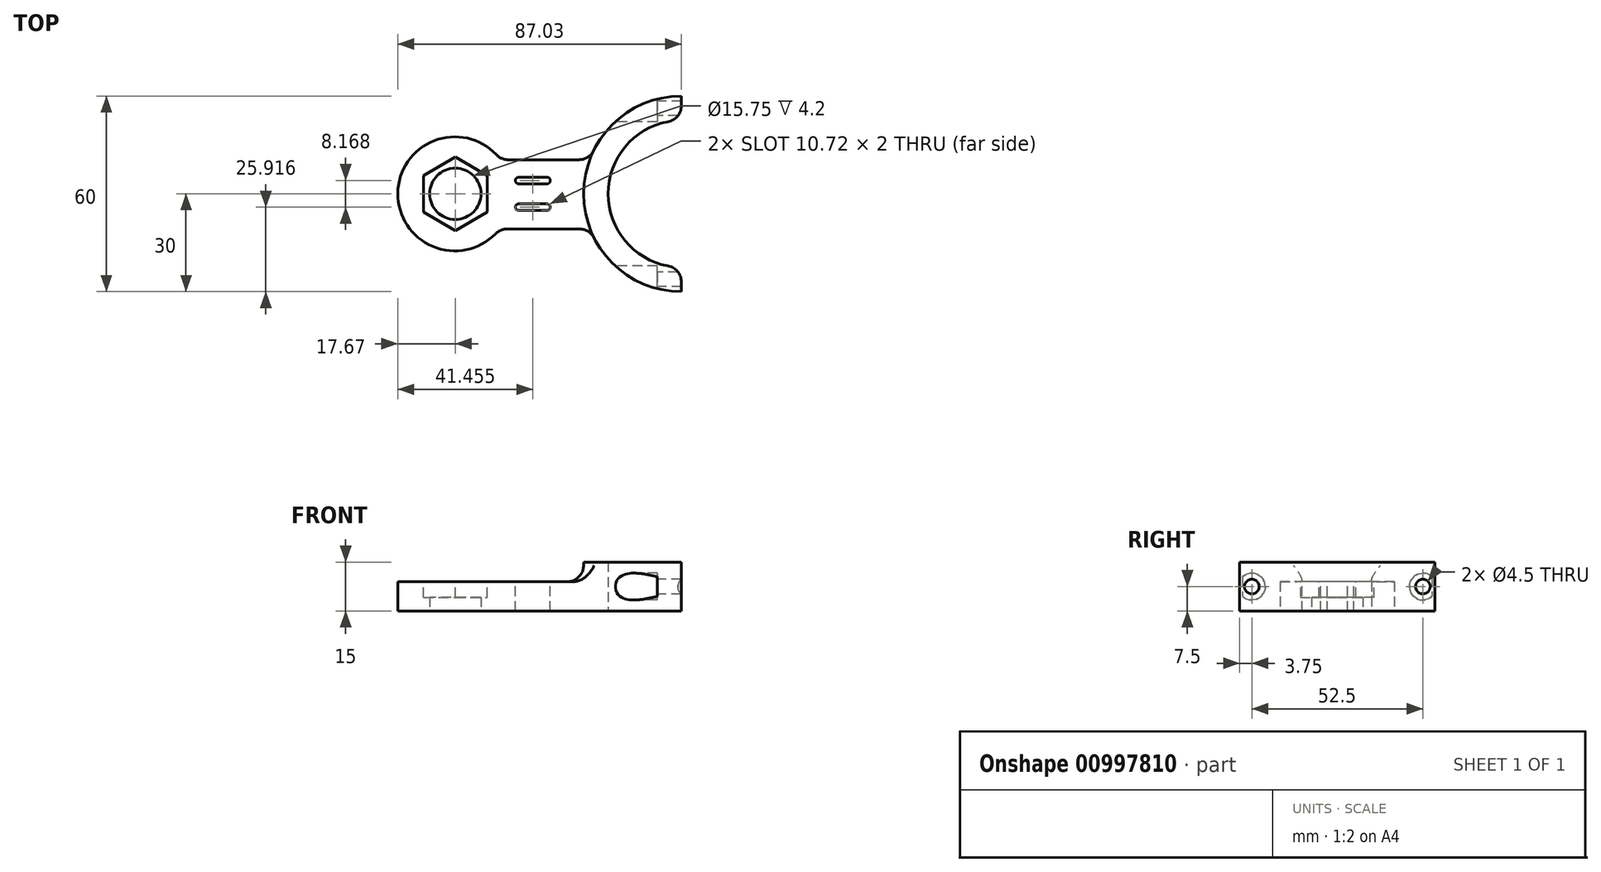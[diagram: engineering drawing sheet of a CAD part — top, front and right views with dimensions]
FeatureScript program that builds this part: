
annotation { "Feature Type Name" : "Feature", "Feature Type Description" : "" }
export const myFeature = defineFeature(function(context is Context, id is Id, definition is map)
    precondition{}
    {
        {
            var Q0;
            Q0=qCreatedBy(makeId("Top.planeOp"),FACE);
            var sketch = newSketch(context, id + "F0", { "sketchPlane" : qUnion([Q0])});
            skCircle(sketch, "E0", {"center": v(0, 0) * mm, "radius": 7.88 * mm});
            skLineSegment(sketch, "E1.top", {"start": v(13.6, -10.8) * mm, "end": v(41.37, -10.8) * mm});
            skArc(sketch, "E2", {"start": v(13.85, 10.47) * mm, "mid": v(-17.67, 0.2) * mm, "end": v(13.6, -10.8) * mm});
            skLineSegment(sketch, "E3", {"start": v(13.85, 10.47) * mm, "end": v(41.25, 10.47) * mm});
            skArc(sketch, "E4", {"start": v(69.36, 22.5) * mm, "mid": v(46.86, 0) * mm, "end": v(69.36, -22.5) * mm});
            skArc(sketch, "E5.0", {"start": v(41.37, -10.8) * mm, "mid": v(52.4, -24.74) * mm, "end": v(69.36, -30) * mm});
            skLineSegment(sketch, "E6", {"start": v(69.36, -22.5) * mm, "end": v(69.36, -30) * mm});
            skLineSegment(sketch, "E7.MirrorCS", {"start": v(69.36, 22.5) * mm, "end": v(69.36, 30) * mm});
            skArc(sketch, "E8.trimOffspring", {"start": v(69.36, 30) * mm, "mid": v(44.63, 16.97) * mm, "end": v(41.37, -10.8) * mm});
            skSolve(sketch);
        }
        {
            var Q0;
            Q0 = qSketchRegion(id + "F0", true);
            extrude(context, id + "F1", {"entities" : qUnion([Q0]), "depth" : 9 * mm, "offsetDistance" : 25 * mm});
        }
        {
            var Q0;
            Q0=makeQuery(id+"F1.opExtrude","CAP_FACE",FACE,{"disambiguationData":[OSD([sQuery(id+"F0.wireOp",EDGE,"E0"),sQuery(id+"F0.wireOp",EDGE,"26NPetrQ-JWbV-A0U1-Rfha-0d6lAM55pXle")])],"isStart":false});
            var sketch = newSketch(context, id + "F2", { "sketchPlane" : qUnion([Q0])});
            skCircle(sketch, "E9.cCircle", {"center": v(0, 0) * mm, "radius": 14.84 * mm, "construction": true});
            skCircle(sketch, "E10.cCircle", {"center": v(0, 0) * mm, "radius": 11.26 * mm, "construction": true});
            skLineSegment(sketch, "E10.0", {"start": v(9.75, 5.63) * mm, "end": v(9.75, -5.63) * mm});
            skLineSegment(sketch, "E10.1", {"start": v(9.75, -5.63) * mm, "end": v(0, -11.26) * mm});
            skLineSegment(sketch, "E10.2", {"start": v(0, -11.26) * mm, "end": v(-9.75, -5.63) * mm});
            skLineSegment(sketch, "E10.3", {"start": v(-9.75, -5.63) * mm, "end": v(-9.75, 5.63) * mm});
            skLineSegment(sketch, "E10.4", {"start": v(-9.75, 5.63) * mm, "end": v(0, 11.26) * mm});
            skLineSegment(sketch, "E10.5", {"start": v(0, 11.26) * mm, "end": v(9.75, 5.63) * mm});
            skSolve(sketch);
        }
        {
            var Q0;
            Q0=makeQuery(id+"F2.imprint","IMPRINT",FACE,{"disambiguationData":[TD([[makeQuery(id+"F2.imprint","IMPRINT",EDGE,{"derivedFrom":sQuery(id+"F2.wireOp",EDGE,"E10.0")}),-1.0]])]});
            extrude(context, id + "F3", {"entities" : qUnion([Q0]), "operationType" : NewBodyOperationType.REMOVE, "oppositeDirection" : true, "depth" : 4.8 * mm, "offsetDistance" : 25 * mm});
        }
        {
            var Q0;
            Q0=makeQuery(id+"F0.imprint","IMPRINT",FACE,{"disambiguationData":[TD([[makeQuery(id+"F0.imprint","IMPRINT",EDGE,{"derivedFrom":sQuery(id+"F0.wireOp",EDGE,"E4")}),-1.0]])]});
            extrude(context, id + "F4", {"entities" : qUnion([Q0]), "operationType" : NewBodyOperationType.ADD, "depth" : 15 * mm, "offsetDistance" : 25 * mm});
        }
        {
            var Q0;
            Q0=makeQuery(id+"F1.opExtrude","SWEPT_EDGE",EDGE,{"disambiguationData":[OSD([sQuery(id+"F0.wireOp",EDGE,"E1.bottom"),sQuery(id+"F0.wireOp",EDGE,"E2")])]});
            var Q1;
            Q1=makeQuery(id+"F1.opExtrude","SWEPT_EDGE",EDGE,{"disambiguationData":[OSD([sQuery(id+"F0.wireOp",EDGE,"E1.top"),sQuery(id+"F0.wireOp",EDGE,"E2")])]});
            var Q2;
            Q2=makeQuery(id+"F1.opExtrude","SWEPT_EDGE",EDGE,{"disambiguationData":[OSD([sQuery(id+"F0.wireOp",EDGE,"E3"),sQuery(id+"F0.wireOp",EDGE,"E8.trimOffspring")])]});
            var Q3;
            Q3=makeQuery(id+"F1.opExtrude","SWEPT_EDGE",EDGE,{"disambiguationData":[OSD([sQuery(id+"F0.wireOp",EDGE,"E1.top"),sQuery(id+"F0.wireOp",EDGE,"E5.0"),sQuery(id+"F0.wireOp",EDGE,"E8.trimOffspring")])]});
            var Q4;
            {var subQ0=sQuery(id+"F0.wireOp",EDGE,"E8.trimOffspring");var subQ1=sQuery(id+"F0.wireOp",EDGE,"E5.0");Q4=makeQuery(id+"F4.boolean.opBoolean","INTERSECT",EDGE,{"derivedFrom":[makeQuery(id+"F1.opExtrude","CAP_FACE",FACE,{"disambiguationData":[OSD([sQuery(id+"F0.wireOp",EDGE,"E0"),sQuery(id+"F0.wireOp",EDGE,"E1.top"),sQuery(id+"F0.wireOp",EDGE,"E2"),sQuery(id+"F0.wireOp",EDGE,"E3"),sQuery(id+"F0.wireOp",EDGE,"E4"),subQ1,sQuery(id+"F0.wireOp",EDGE,"E6"),sQuery(id+"F0.wireOp",EDGE,"E7.MirrorCS"),subQ0])],"isStart":false}),makeQuery(id+"F4.opExtrude","SWEPT_FACE",FACE,{"disambiguationData":[OSD([subQ1,subQ0])]})]});}
            fillet(context, id + "F5", {"entities" : qUnion([Q0, Q1, Q2, Q3, Q4]), "radius" : 5 * mm, "tangentPropagation" : true, "allowEdgeOverflow" : false});
        }
        {
            var Q0;
            {var subQ0=sQuery(id+"F0.wireOp",EDGE,"E7.MirrorCS");Q0=makeQuery(id+"F4.boolean.opBoolean","MERGE",FACE,{"derivedFrom":[makeQuery(id+"F1.opExtrude","SWEPT_FACE",FACE,{"disambiguationData":[OSD([subQ0])]}),makeQuery(id+"F4.opExtrude","SWEPT_FACE",FACE,{"disambiguationData":[OSD([subQ0])]})]});}
            cPlane(context, id + "F6", {"entities" : qUnion([Q0]), "cplaneType" : CPlaneType.OFFSET, "offset" : 24.4 * mm, "oppositeDirection" : true, "width" : 150 * mm, "height" : 150 * mm});
        }
        {
            var Q0;
            Q0=qCreatedBy(id+"F6.planeOp",FACE);
            var sketch = newSketch(context, id + "F7", { "sketchPlane" : qUnion([Q0])});
            skPoint(sketch, "E11", {"position": v(-26.25, 7.5) * mm});
            skPoint(sketch, "E11.positionSnap0", {"position": v(-26.25, 15) * mm});
            skPoint(sketch, "E11.positionSnap1", {"position": v(-30, 7.5) * mm});
            skPoint(sketch, "E12.MirrorP", {"position": v(26.25, 7.5) * mm});
            skSolve(sketch);
        }
        {
            var Q0;
            Q0=sQuery(id+"F7.wireOp",VERTEX,"E12.MirrorP");
            var Q1;
            Q1=sQuery(id+"F7.wireOp",VERTEX,"E11");
            var Q2;
            Q2=makeQuery(id+"F1.opExtrude","SWEPT_BODY",BODY,{"disambiguationData":[OSD([sQuery(id+"F0.wireOp",EDGE,"E0"),sQuery(id+"F0.wireOp",EDGE,"E1.top"),sQuery(id+"F0.wireOp",EDGE,"E2"),sQuery(id+"F0.wireOp",EDGE,"E3"),sQuery(id+"F0.wireOp",EDGE,"E4"),sQuery(id+"F0.wireOp",EDGE,"E5.0"),sQuery(id+"F0.wireOp",EDGE,"E6"),sQuery(id+"F0.wireOp",EDGE,"E7.MirrorCS"),sQuery(id+"F0.wireOp",EDGE,"E8.trimOffspring")])]});
            hole(context, id + "F8", {"style" : HoleStyle.C_BORE, "endStyle" : HoleEndStyle.BLIND, "oppositeDirection" : true, "holeDiameter" : 4.5 * mm, "cBoreDiameter" : 8.25 * mm, "cBoreDepth" : 17 * mm, "majorDiameter" : 5 * mm, "holeDepth" : 25 * mm, "isTappedThrough" : true, "tappedDepth" : 12 * mm, "tapClearance" : 3, "startFromSketch" : true, "locations" : qUnion([Q0, Q1]), "scope" : qUnion([Q2])});
        }
        {
            var Q0;
            {var subQ0=sQuery(id+"F0.wireOp",EDGE,"E7.MirrorCS");var subQ1=sQuery(id+"F0.wireOp",EDGE,"E4");Q0=makeQuery(id+"F4.boolean.opBoolean","MERGE",EDGE,{"derivedFrom":[makeQuery(id+"F1.opExtrude","SWEPT_EDGE",EDGE,{"disambiguationData":[OSD([subQ1,subQ0])]}),makeQuery(id+"F4.opExtrude","SWEPT_EDGE",EDGE,{"disambiguationData":[OSD([subQ1,subQ0])]})]});}
            var Q1;
            {var subQ0=sQuery(id+"F0.wireOp",EDGE,"E6");var subQ1=sQuery(id+"F0.wireOp",EDGE,"E4");Q1=makeQuery(id+"F4.boolean.opBoolean","MERGE",EDGE,{"derivedFrom":[makeQuery(id+"F1.opExtrude","SWEPT_EDGE",EDGE,{"disambiguationData":[OSD([subQ1,subQ0])]}),makeQuery(id+"F4.opExtrude","SWEPT_EDGE",EDGE,{"disambiguationData":[OSD([subQ1,subQ0])]})]});}
            fillet(context, id + "F9", {"entities" : qUnion([Q0, Q1]), "radius" : 5 * mm, "tangentPropagation" : true, "allowEdgeOverflow" : false});
        }
        {
            var Q0;
            Q0=makeQuery(id+"F1.opExtrude","CAP_FACE",FACE,{"disambiguationData":[OSD([sQuery(id+"F0.wireOp",EDGE,"E0"),sQuery(id+"F0.wireOp",EDGE,"E1.top"),sQuery(id+"F0.wireOp",EDGE,"E2"),sQuery(id+"F0.wireOp",EDGE,"E3"),sQuery(id+"F0.wireOp",EDGE,"E4"),sQuery(id+"F0.wireOp",EDGE,"E5.0"),sQuery(id+"F0.wireOp",EDGE,"E6"),sQuery(id+"F0.wireOp",EDGE,"E7.MirrorCS"),sQuery(id+"F0.wireOp",EDGE,"E8.trimOffspring")])],"isStart":false});
            var sketch = newSketch(context, id + "F10", { "sketchPlane" : qUnion([Q0])});
            skLineSegment(sketch, "E13", {"start": v(19.43, 4.08) * mm, "end": v(28.14, 4.08) * mm});
            skArc(sketch, "E14.0.startCap", {"start": v(19.43, 3.08) * mm, "mid": v(18.43, 4.08) * mm, "end": v(19.43, 5.08) * mm});
            skArc(sketch, "E14.0.endCap", {"start": v(28.14, 5.08) * mm, "mid": v(29.14, 4.08) * mm, "end": v(28.14, 3.08) * mm});
            skLineSegment(sketch, "E14.0.left", {"start": v(19.43, 5.08) * mm, "end": v(28.14, 5.08) * mm});
            skLineSegment(sketch, "E14.0.right", {"start": v(19.43, 3.08) * mm, "end": v(28.14, 3.08) * mm});
            skArc(sketch, "E15.MirrorCS", {"start": v(19.43, -3.08) * mm, "mid": v(18.43, -4.08) * mm, "end": v(19.43, -5.08) * mm});
            skLineSegment(sketch, "E16.MirrorCS", {"start": v(19.43, -4.08) * mm, "end": v(28.14, -4.08) * mm});
            skArc(sketch, "E17.MirrorCS", {"start": v(28.14, -5.08) * mm, "mid": v(29.14, -4.08) * mm, "end": v(28.14, -3.08) * mm});
            skLineSegment(sketch, "E18.MirrorCS", {"start": v(19.43, -3.08) * mm, "end": v(28.14, -3.08) * mm});
            skLineSegment(sketch, "E19.MirrorCS", {"start": v(19.43, -5.08) * mm, "end": v(28.14, -5.08) * mm});
            skSolve(sketch);
        }
        {
            var Q0;
            Q0 = qSketchRegion(id + "F10", true);
            extrude(context, id + "F11", {"entities" : qUnion([Q0]), "operationType" : NewBodyOperationType.REMOVE, "oppositeDirection" : true, "depth" : 25 * mm, "offsetDistance" : 25 * mm});
        }
    });
